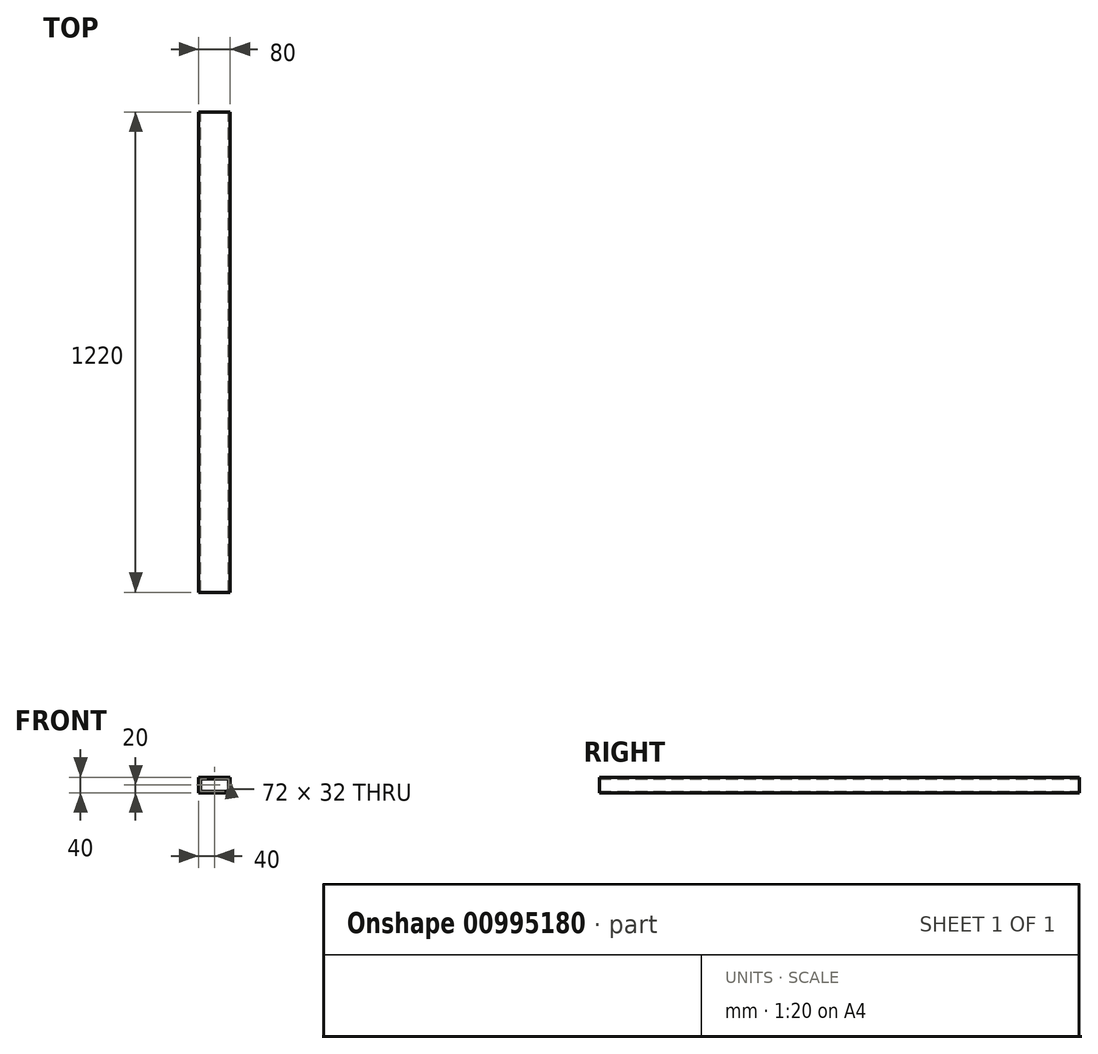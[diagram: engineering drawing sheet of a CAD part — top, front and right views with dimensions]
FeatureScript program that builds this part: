
annotation { "Feature Type Name" : "Feature", "Feature Type Description" : "" }
export const myFeature = defineFeature(function(context is Context, id is Id, definition is map)
    precondition{}
    {
        {
            var Q0;
            Q0=qCreatedBy(makeId("Front.planeOp"),FACE);
            var sketch = newSketch(context, id + "F0", { "sketchPlane" : qUnion([Q0])});
            skLineSegment(sketch, "E0.bottom", {"start": v(-40, 20) * mm, "end": v(40, 20) * mm});
            skLineSegment(sketch, "E0.top", {"start": v(-40, -20) * mm, "end": v(40, -20) * mm});
            skLineSegment(sketch, "E0.left", {"start": v(-40, 20) * mm, "end": v(-40, -20) * mm});
            skLineSegment(sketch, "E0.right", {"start": v(40, 20) * mm, "end": v(40, -20) * mm});
            skPoint(sketch, "E0.middle", {"position": v(0, 0) * mm});
            skLineSegment(sketch, "E1.0", {"start": v(-36, 16) * mm, "end": v(36, 16) * mm});
            skLineSegment(sketch, "E1.1", {"start": v(-36, 16) * mm, "end": v(-36, -16) * mm});
            skLineSegment(sketch, "E1.2", {"start": v(-36, -16) * mm, "end": v(36, -16) * mm});
            skLineSegment(sketch, "E1.3", {"start": v(36, 16) * mm, "end": v(36, -16) * mm});
            skSolve(sketch);
        }
        {
            var Q0;
            Q0=makeQuery(id+"F0.imprint","IMPRINT",FACE,{"disambiguationData":[TD([[makeQuery(id+"F0.imprint","IMPRINT",EDGE,{"derivedFrom":sQuery(id+"F0.wireOp",EDGE,"E0.bottom")}),-1.0]])]});
            extrude(context, id + "F1", {"entities" : qUnion([Q0]), "depth" : 1220 * mm, "offsetDistance" : 25 * mm, "symmetric" : true});
        }
    });
